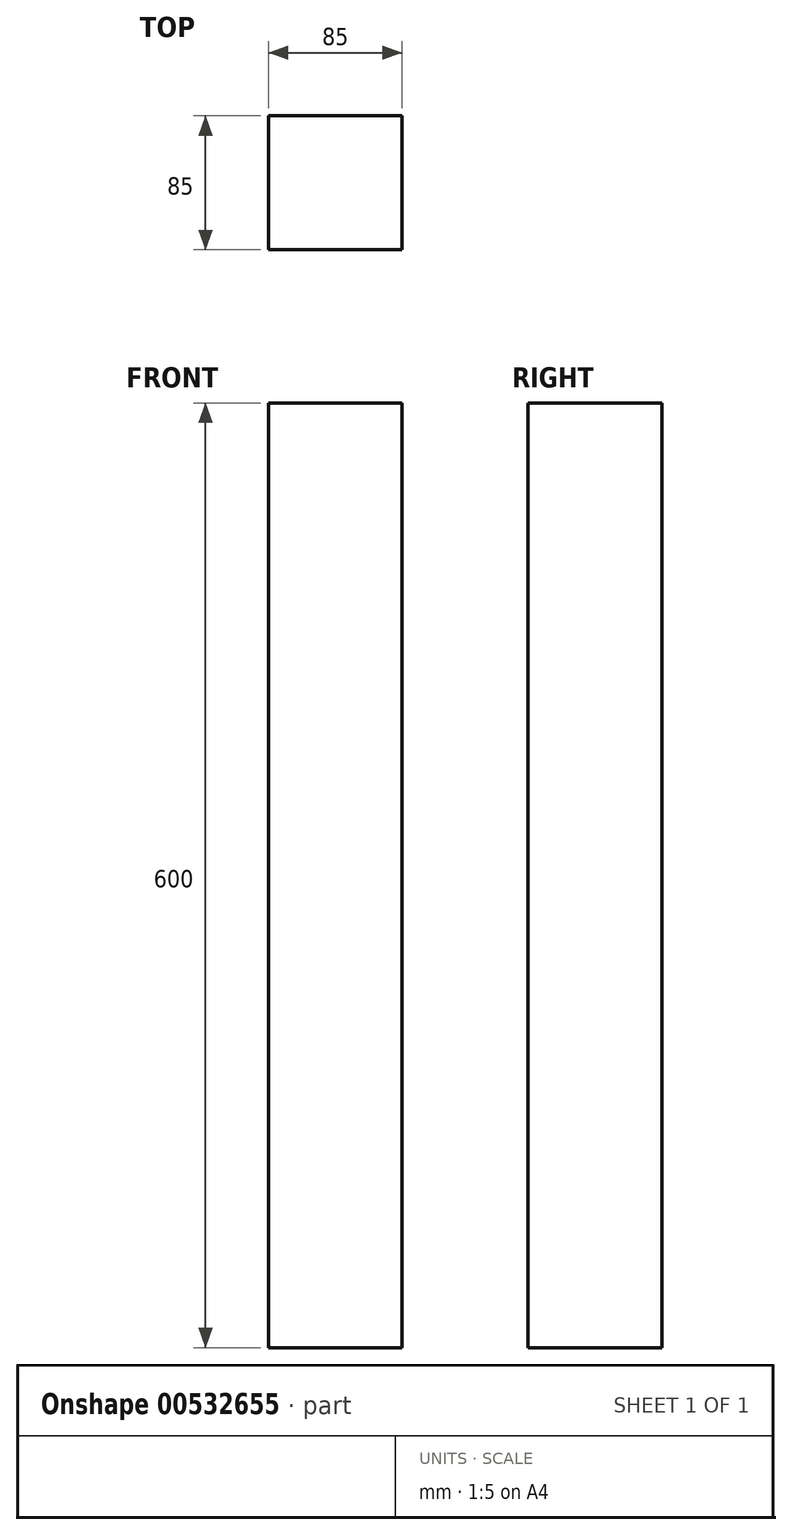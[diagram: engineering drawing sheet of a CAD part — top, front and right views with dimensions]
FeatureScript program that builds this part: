
annotation { "Feature Type Name" : "Feature", "Feature Type Description" : "" }
export const myFeature = defineFeature(function(context is Context, id is Id, definition is map)
    precondition{}
    {
        {
            var Q0;
            Q0=qCreatedBy(makeId("Top.planeOp"),FACE);
            var sketch = newSketch(context, id + "F0", { "sketchPlane" : qUnion([Q0])});
            skLineSegment(sketch, "E0.bottom", {"start": v(-50.27, 48.93) * mm, "end": v(34.73, 48.93) * mm});
            skLineSegment(sketch, "E0.top", {"start": v(-50.27, -36.07) * mm, "end": v(34.73, -36.07) * mm});
            skLineSegment(sketch, "E0.left", {"start": v(-50.27, 48.93) * mm, "end": v(-50.27, -36.07) * mm});
            skLineSegment(sketch, "E0.right", {"start": v(34.73, 48.93) * mm, "end": v(34.73, -36.07) * mm});
            skSolve(sketch);
        }
        {
            var Q0;
            Q0 = qSketchRegion(id + "F0", true);
            extrude(context, id + "F1", {"entities" : qUnion([Q0]), "oppositeDirection" : true, "depth" : 600 * mm, "offsetDistance" : 25 * mm});
        }
    });
